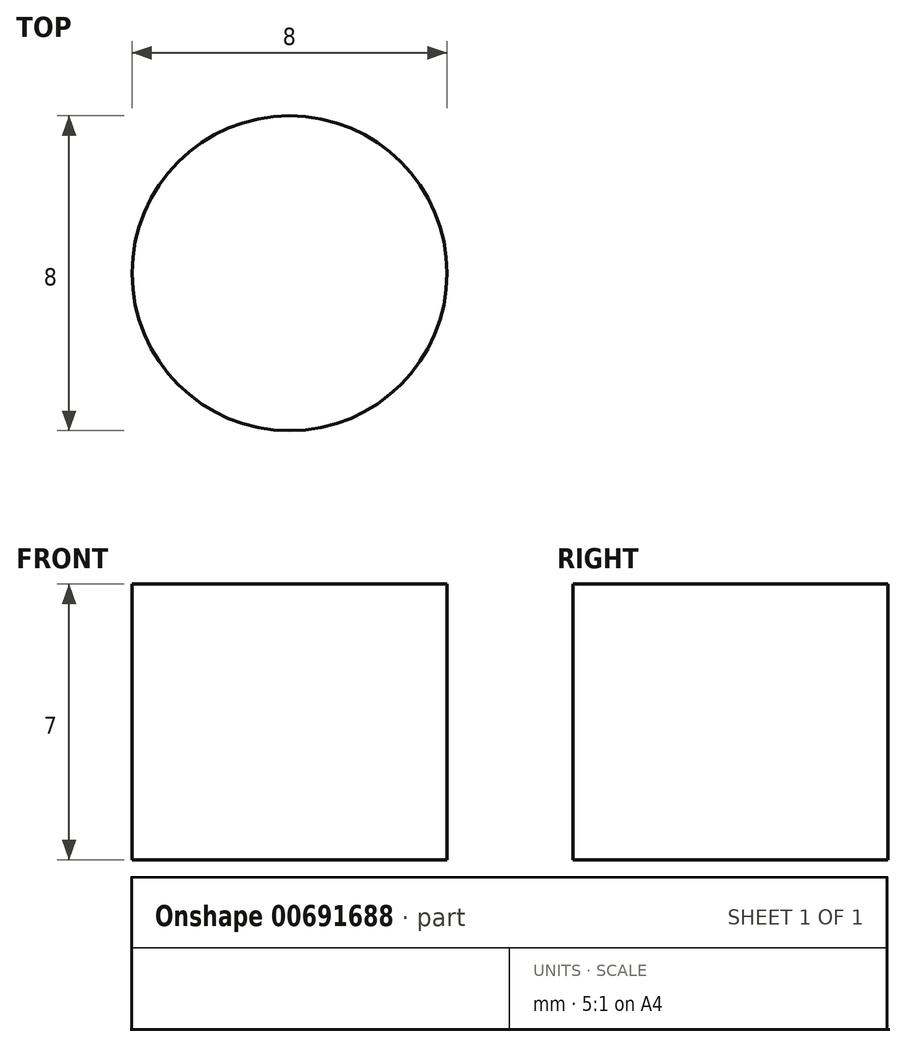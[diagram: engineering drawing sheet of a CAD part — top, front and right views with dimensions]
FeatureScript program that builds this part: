
annotation { "Feature Type Name" : "Feature", "Feature Type Description" : "" }
export const myFeature = defineFeature(function(context is Context, id is Id, definition is map)
    precondition{}
    {
        {
            var Q0;
            Q0=qCreatedBy(makeId("Top.planeOp"),FACE);
            var sketch = newSketch(context, id + "F0", { "sketchPlane" : qUnion([Q0])});
            skCircle(sketch, "E0", {"center": v(0, 0) * mm, "radius": 4 * mm});
            skSolve(sketch);
        }
        {
            var Q0;
            Q0 = qSketchRegion(id + "F0", true);
            extrude(context, id + "F1", {"entities" : qUnion([Q0]), "depth" : 7 * mm, "offsetDistance" : 25 * mm});
        }
    });
